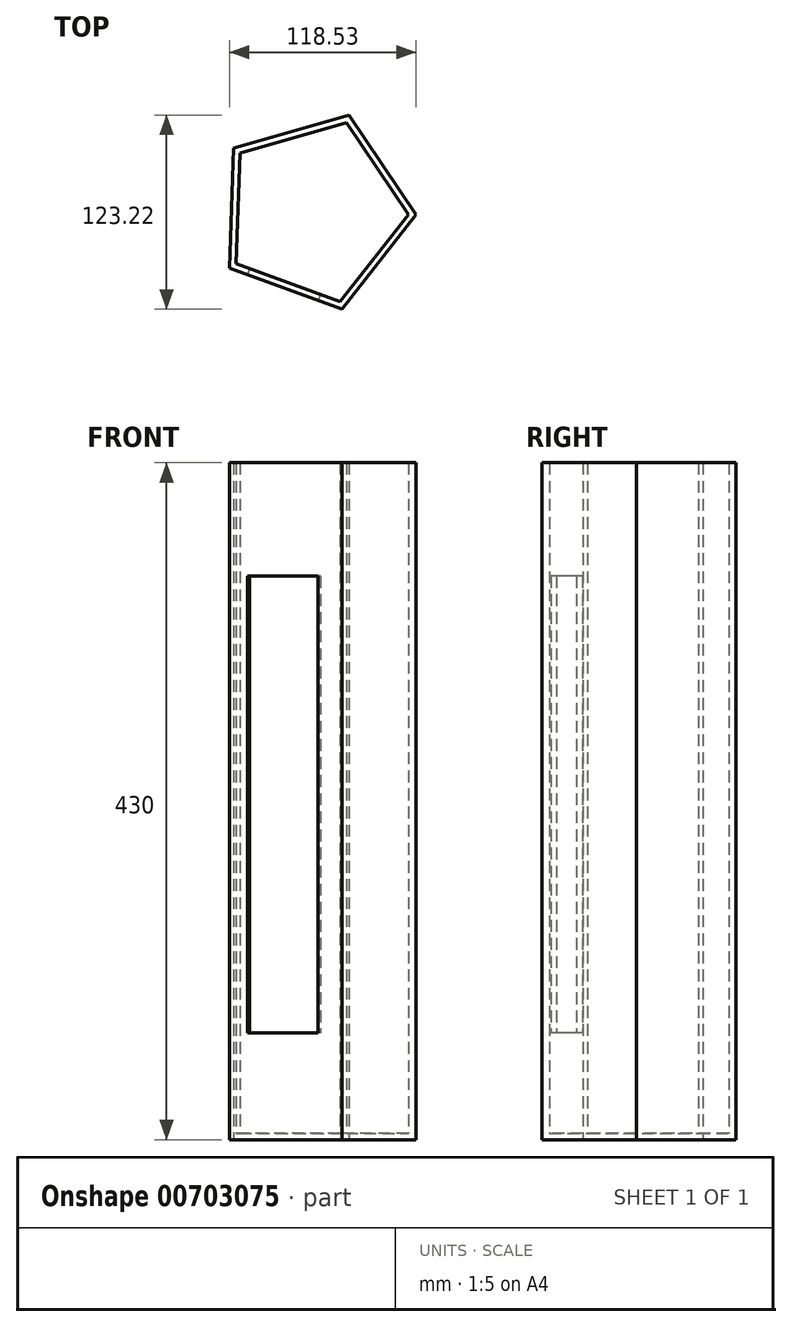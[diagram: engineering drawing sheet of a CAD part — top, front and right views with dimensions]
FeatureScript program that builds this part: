
annotation { "Feature Type Name" : "Feature", "Feature Type Description" : "" }
export const myFeature = defineFeature(function(context is Context, id is Id, definition is map)
    precondition{}
    {
        {
            var Q0;
            Q0=qCreatedBy(makeId("Top.planeOp"),FACE);
            var sketch = newSketch(context, id + "F0", { "sketchPlane" : qUnion([Q0])});
            skCircle(sketch, "E0.cCircle", {"center": v(0, 0) * mm, "radius": 52.44 * mm, "construction": true});
            skLineSegment(sketch, "E0.0", {"start": v(64.78, -2.29) * mm, "end": v(17.84, -62.32) * mm});
            skLineSegment(sketch, "E0.1", {"start": v(17.84, -62.32) * mm, "end": v(-53.75, -36.22) * mm});
            skLineSegment(sketch, "E0.2", {"start": v(-53.75, -36.22) * mm, "end": v(-51.06, 39.93) * mm});
            skLineSegment(sketch, "E0.3", {"start": v(-51.06, 39.93) * mm, "end": v(22.2, 60.9) * mm});
            skLineSegment(sketch, "E0.4", {"start": v(22.2, 60.9) * mm, "end": v(64.78, -2.29) * mm});
            skPoint(sketch, "E0.0.midPoint", {"position": v(41.3, -32.3) * mm});
            skSolve(sketch);
        }
        {
            var Q0;
            Q0 = qSketchRegion(id + "F0", true);
            extrude(context, id + "F1", {"entities" : qUnion([Q0]), "depth" : 430 * mm, "offsetDistance" : 25.4 * mm});
        }
        {
            var Q0;
            Q0=makeQuery(id+"F1.opExtrude","CAP_FACE",FACE,{"disambiguationData":[OSD([sQuery(id+"F0.wireOp",EDGE,"E0.0"),sQuery(id+"F0.wireOp",EDGE,"E0.1"),sQuery(id+"F0.wireOp",EDGE,"E0.2"),sQuery(id+"F0.wireOp",EDGE,"E0.3"),sQuery(id+"F0.wireOp",EDGE,"E0.4")])],"isStart":false});
            shell(context, id + "F2", {"entities" : qUnion([Q0]), "thickness" : 4 * mm});
        }
        {
            var Q0;
            Q0=makeQuery(id+"F1.opExtrude","SWEPT_FACE",FACE,{"disambiguationData":[OSD([sQuery(id+"F0.wireOp",EDGE,"E0.1")])]});
            var sketch = newSketch(context, id + "F3", { "sketchPlane" : qUnion([Q0])});
            skLineSegment(sketch, "E1.bottom", {"start": v(-26, 358.03) * mm, "end": v(21.93, 358.03) * mm});
            skLineSegment(sketch, "E1.top", {"start": v(-26, 67.8) * mm, "end": v(21.93, 67.8) * mm});
            skLineSegment(sketch, "E1.left", {"start": v(-26, 358.03) * mm, "end": v(-26, 67.8) * mm});
            skLineSegment(sketch, "E1.right", {"start": v(21.93, 358.03) * mm, "end": v(21.93, 67.8) * mm});
            skSolve(sketch);
        }
        {
            var Q0;
            Q0 = qSketchRegion(id + "F3", true);
            extrude(context, id + "F4", {"entities" : qUnion([Q0]), "operationType" : NewBodyOperationType.REMOVE, "oppositeDirection" : true, "depth" : 12.7 * mm, "offsetDistance" : 25.4 * mm});
        }
    });
